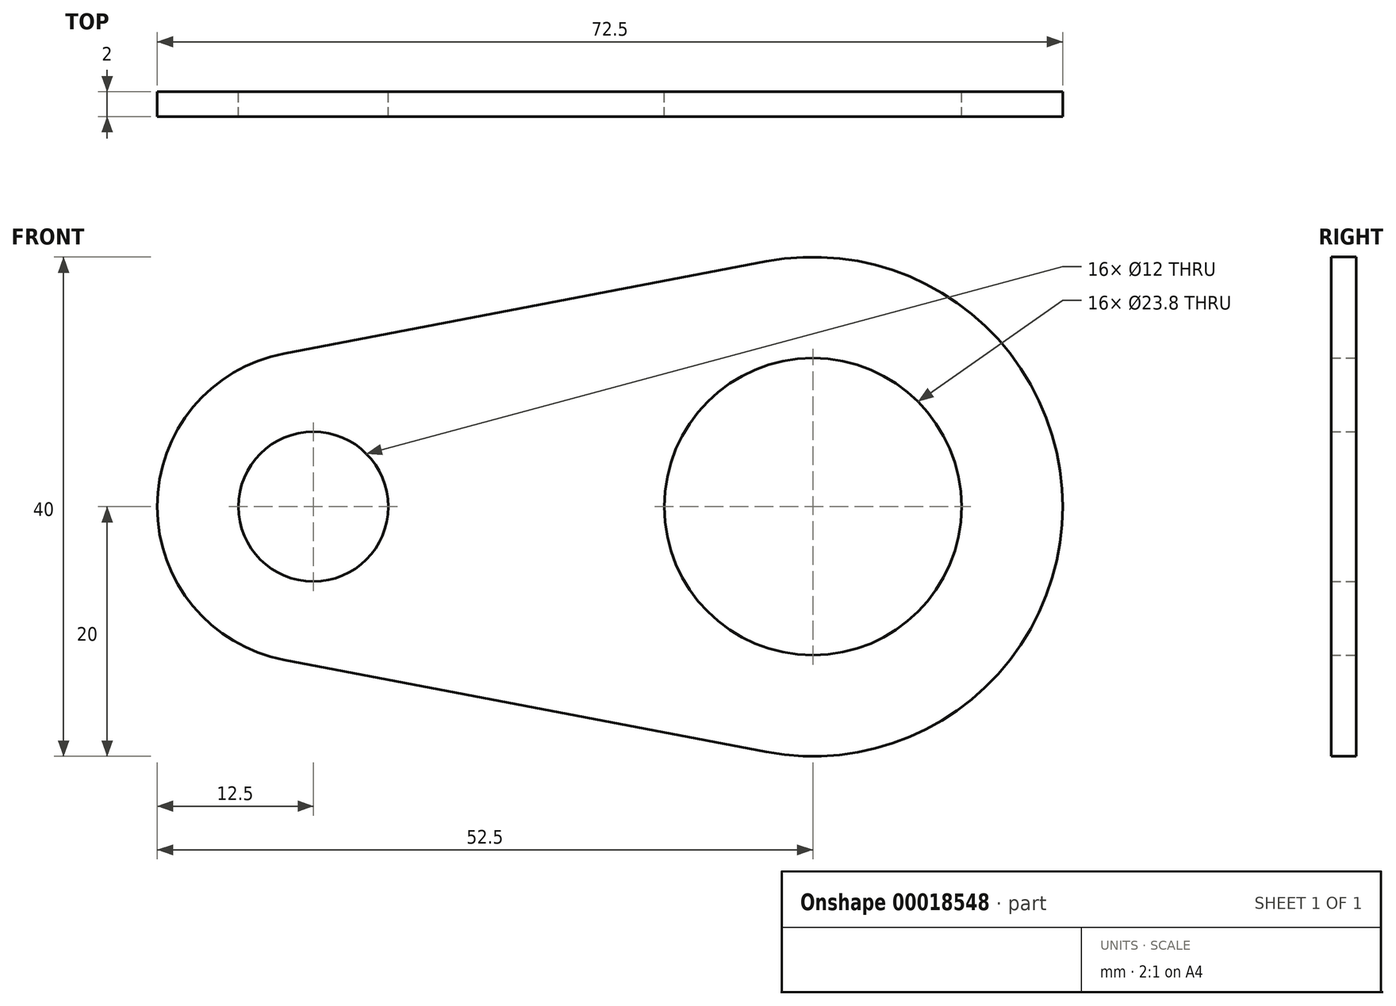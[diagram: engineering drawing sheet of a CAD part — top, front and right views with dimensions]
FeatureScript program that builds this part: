
annotation { "Feature Type Name" : "Feature", "Feature Type Description" : "" }
export const myFeature = defineFeature(function(context is Context, id is Id, definition is map)
    precondition{}
    {
        {
            var Q0;
            Q0=qCreatedBy(makeId("Front.planeOp"),FACE);
            var sketch = newSketch(context, id + "F0", { "sketchPlane" : qUnion([Q0])});
            skCircle(sketch, "E0", {"center": v(0, 0) * mm, "radius": 6 * mm});
            skCircle(sketch, "E1", {"center": v(40, 0) * mm, "radius": 11.9 * mm});
            skCircle(sketch, "E2", {"center": v(40, 0) * mm, "radius": 20 * mm});
            skCircle(sketch, "E3", {"center": v(0, 0) * mm, "radius": 12.5 * mm});
            skLineSegment(sketch, "E4", {"start": v(0, 0) * mm, "end": v(40, 0) * mm, "construction": true});
            skLineSegment(sketch, "E5", {"start": v(-2.34, 12.28) * mm, "end": v(36.25, 19.65) * mm});
            skLineSegment(sketch, "E6.MirrorCS", {"start": v(-2.34, -12.28) * mm, "end": v(36.25, -19.65) * mm});
            skSolve(sketch);
        }
        {
            var Q0;
            Q0=makeQuery(id+"F0.imprint","IMPRINT",FACE,{"disambiguationData":[TD([[makeQuery(id+"F0.imprint","IMPRINT",EDGE,{"derivedFrom":sQuery(id+"F0.wireOp",EDGE,"E0")}),-1.0]])]});
            var Q1;
            {var subQ0=sQuery(id+"F0.wireOp",EDGE,"E5");Q1=makeQuery(id+"F0.imprint","IMPRINT",FACE,{"disambiguationData":[TD([[makeQuery(id+"F0.imprint","IMPRINT",EDGE,{"derivedFrom":subQ0}),-1.0]])]});}
            var Q2;
            Q2=makeQuery(id+"F0.imprint","IMPRINT",FACE,{"disambiguationData":[TD([[makeQuery(id+"F0.imprint","IMPRINT",EDGE,{"derivedFrom":sQuery(id+"F0.wireOp",EDGE,"E1")}),-1.0]])]});
            extrude(context, id + "F1", {"entities" : qUnion([Q0, Q1, Q2]), "depth" : 2 * mm});
        }
    });
